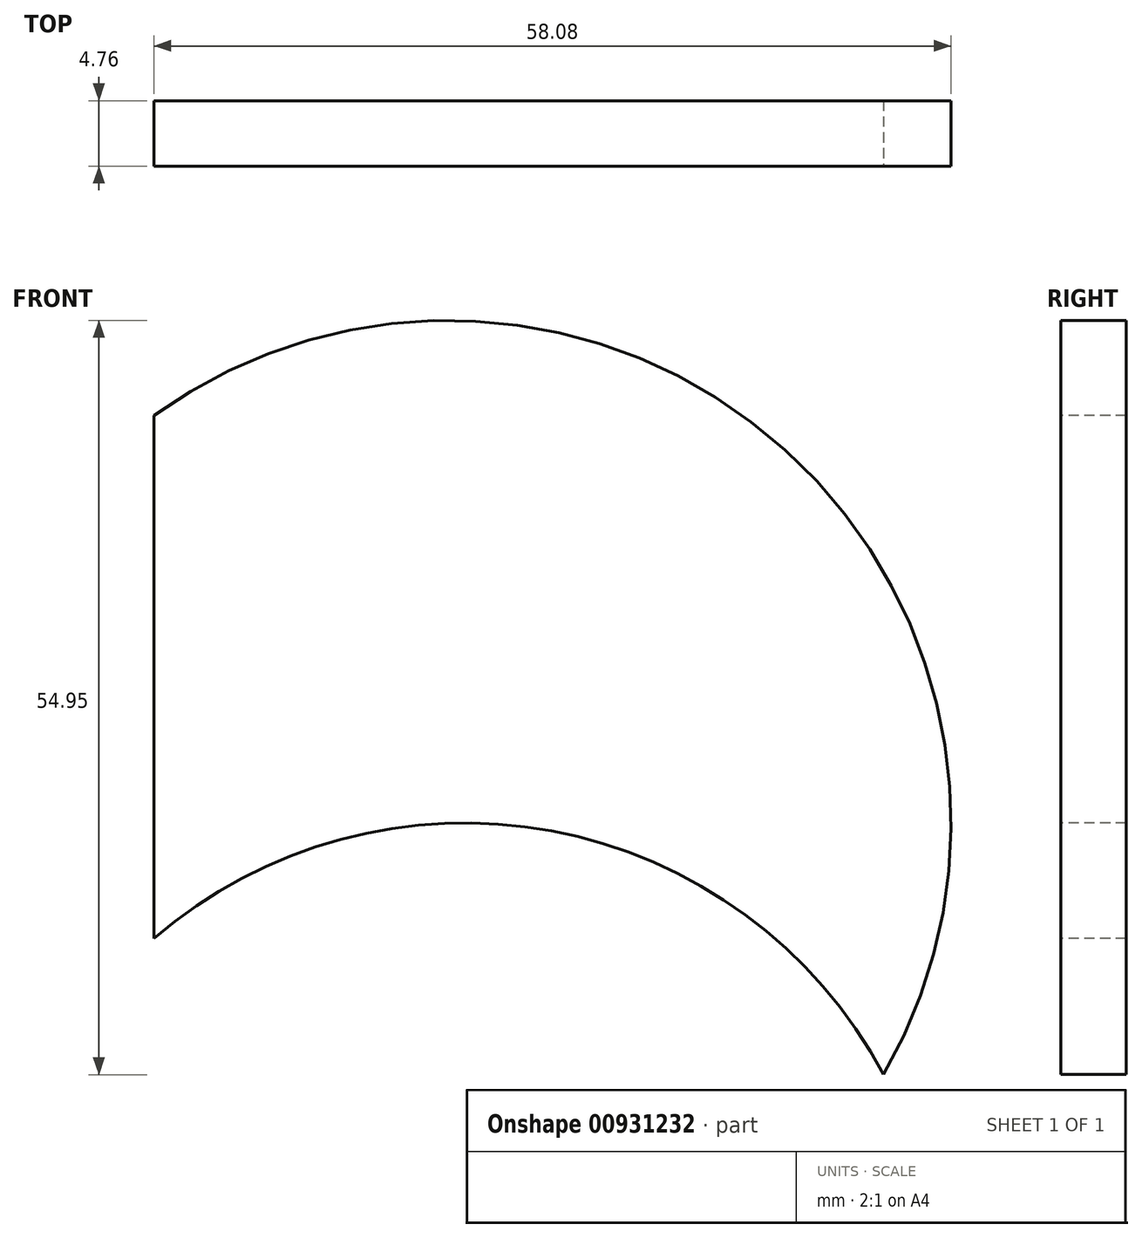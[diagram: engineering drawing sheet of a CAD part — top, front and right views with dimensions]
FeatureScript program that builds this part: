
annotation { "Feature Type Name" : "Feature", "Feature Type Description" : "" }
export const myFeature = defineFeature(function(context is Context, id is Id, definition is map)
    precondition{}
    {
        {
            var Q0;
            Q0=qCreatedBy(makeId("Front.planeOp"),FACE);
            var sketch = newSketch(context, id + "F0", { "sketchPlane" : qUnion([Q0])});
            skCircle(sketch, "E0", {"center": v(0, 0) * mm, "radius": 36.63 * mm});
            skLineSegment(sketch, "E1", {"start": v(0, 0) * mm, "end": v(47.31, -27.32) * mm});
            skLineSegment(sketch, "E2", {"start": v(0, 0) * mm, "end": v(47.31, 0) * mm});
            skLineSegment(sketch, "E3", {"start": v(-21.45, 29.7) * mm, "end": v(-21.45, -8.4) * mm});
            skCircle(sketch, "E4", {"center": v(1.18, -34.59) * mm, "radius": 34.6 * mm});
            skPoint(sketch, "E4.second.point", {"position": v(31.72, -18.32) * mm});
            skSolve(sketch);
        }
        {
            var Q0;
            {var subQ4=sQuery(id+"F0.wireOp",EDGE,"E3");Q0=makeQuery(id+"F0.imprint","IMPRINT",FACE,{"disambiguationData":[TD([[makeQuery(id+"F0.imprint","IMPRINT",EDGE,{"derivedFrom":subQ4}),1.0]])]});}
            var Q1;
            {var subQ0=sQuery(id+"F0.wireOp",EDGE,"E2");var subQ1=sQuery(id+"F0.wireOp",EDGE,"E0");var subQ2=makeQuery(id+"F0.imprint","INTERSECT",VERTEX,{"derivedFrom":[subQ1,subQ0]});Q1=makeQuery(id+"F0.imprint","IMPRINT",FACE,{"disambiguationData":[TD([[makeQuery(id+"F0.imprint","IMPRINT",EDGE,{"disambiguationData":[TD([[subQ2,1.0]])],"derivedFrom":subQ0}),-1.0]])]});}
            extrude(context, id + "F1", {"entities" : qUnion([Q0, Q1]), "oppositeDirection" : true, "depth" : 4.76 * mm, "offsetDistance" : 25.4 * mm});
        }
    });
